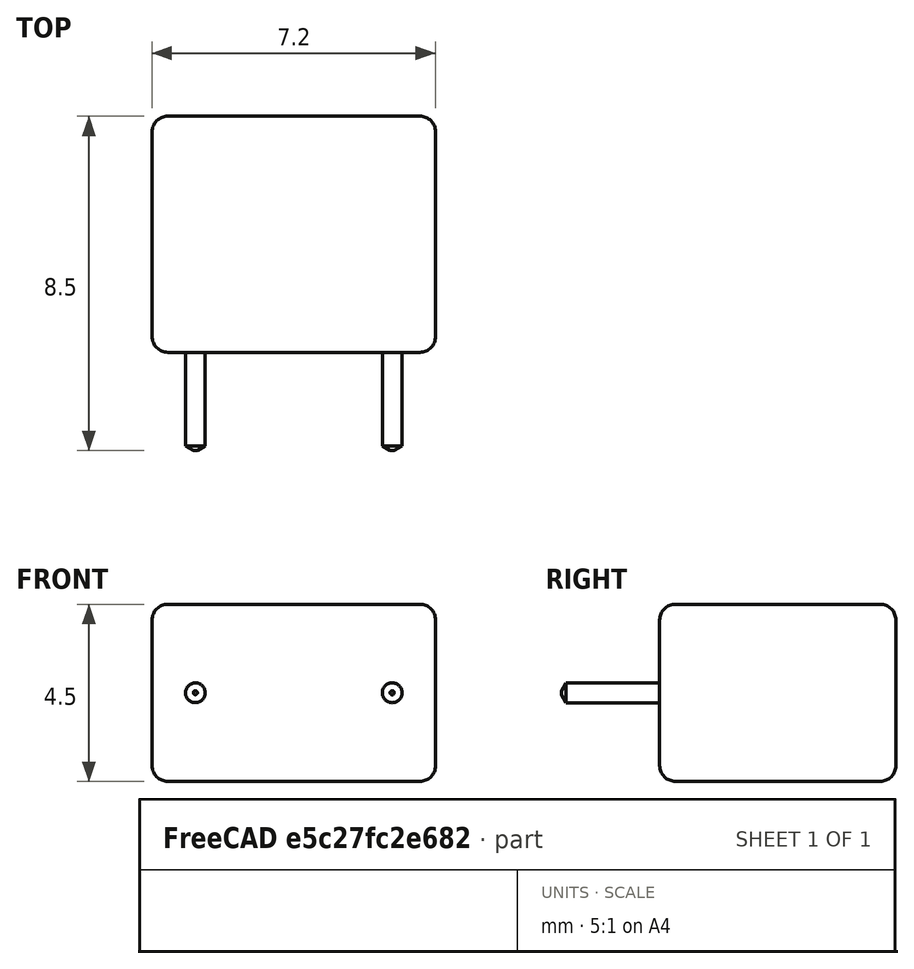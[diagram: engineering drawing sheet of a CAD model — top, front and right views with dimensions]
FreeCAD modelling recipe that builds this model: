
FCSTD DOCUMENT  (FreeCAD 0.17R13528 (Git))
Label: WIMA_D_Case
License: All rights reserved
LicenseURL: http://en.wikipedia.org/wiki/All_rights_reserved
objects: Part::Part2DObjectPython×6, Part::Feature×1
note: 7 computed .brp shape members not serialized (recipe doc carries the construction recipe); baked Part::Feature solids carry a one-line shape summary decoded from their .brp

FEATURE [Part::Feature] Part__Feature  label="WIMA_D_Case"
  shape: bbox 7.2 x 8.5 x 4.5 mm, 36 faces (baked)
FEATURE [Part::Part2DObjectPython] ShapeString  label="F_WIMA"  # Draft 2D object (typed FeaturePython)
  FontFile = <userpath>/Desktop/Freecad Projects/calibrib.ttf
  Placement = pos=(-0.75,3.5,2.26) rot=(0,0,1;0rad)
  Size = 1.75
  String = WIMA
  Support = -> [Part__Feature]
  Tracking = 0
FEATURE [Part::Part2DObjectPython] ShapeString001  label="F_Vaule/Rating"  # Draft 2D object (typed FeaturePython)
  FontFile = <userpath>/Desktop/Freecad Projects/calibrib.ttf
  Placement = pos=(-0.65,2.25,2.26) rot=(0,0,1;0rad)
  Size = 1
  String = 680/630V
  Support = -> [Part__Feature]
  Tracking = 0
FEATURE [Part::Part2DObjectPython] ShapeString002  label="F_Tolerance"  # Draft 2D object (typed FeaturePython)
  FontFile = <userpath>/Desktop/Freecad Projects/calibrib.ttf
  Placement = pos=(-0.65,1,2.26) rot=(0,0,1;0rad)
  Size = 1
  String = 5
  Support = -> [Part__Feature]
  Tracking = 0
FEATURE [Part::Part2DObjectPython] ShapeString003  label="B_WIMA"  # Draft 2D object (typed FeaturePython)
  FontFile = <userpath>/Desktop/Freecad Projects/calibrib.ttf
  Placement = pos=(5,3.5,-2.26) rot=(0,1,0;3.14159rad)
  Size = 1.75
  String = WIMA
  Support = -> [Part__Feature]
  Tracking = 0
FEATURE [Part::Part2DObjectPython] ShapeString004  label="B_Value/Tolerance"  # Draft 2D object (typed FeaturePython)
  FontFile = <userpath>/Desktop/Freecad Projects/calibrib.ttf
  Placement = pos=(4.9,2.25,-2.26) rot=(0,1,0;3.14159rad)
  Size = 1
  String = 680/630V
  Support = -> [Part__Feature]
  Tracking = 0
FEATURE [Part::Part2DObjectPython] ShapeString005  label="B_Tolerance"  # Draft 2D object (typed FeaturePython)
  FontFile = <userpath>/Desktop/Freecad Projects/calibrib.ttf
  Placement = pos=(4.9,1,-2.26) rot=(0,1,0;3.14159rad)
  Size = 1
  String = 5
  Support = -> [Part__Feature]
  Tracking = 0
